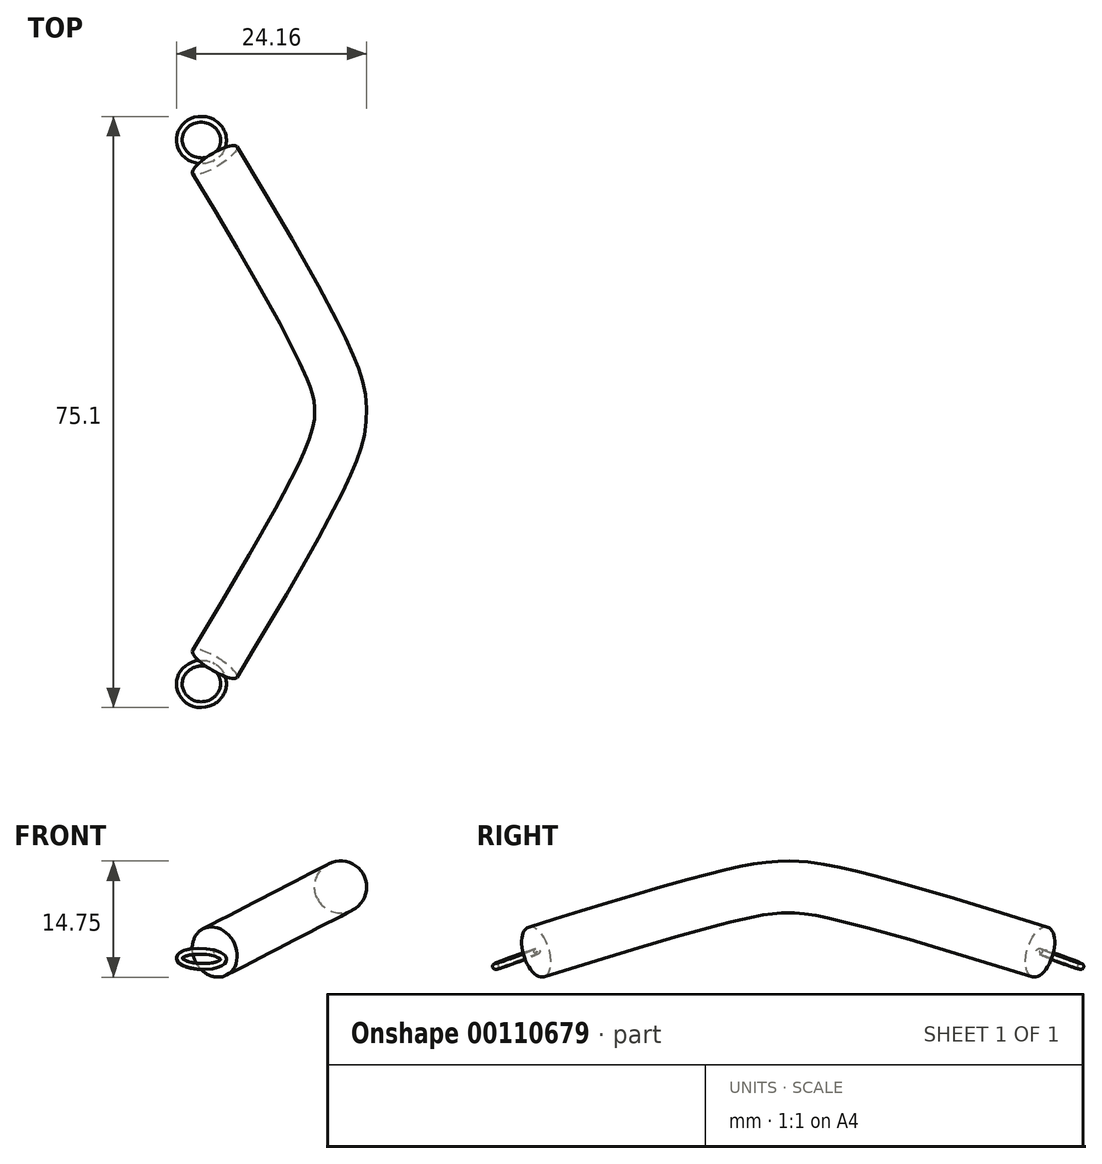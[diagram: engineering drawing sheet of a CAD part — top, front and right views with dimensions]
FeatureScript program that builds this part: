
annotation { "Feature Type Name" : "Feature", "Feature Type Description" : "" }
export const myFeature = defineFeature(function(context is Context, id is Id, definition is map)
    precondition{}
    {
        {
            var Q0;
            Q0=qCreatedBy(makeId("Top.planeOp"),FACE);
            var sketch = newSketch(context, id + "F0", { "sketchPlane" : qUnion([Q0])});
            skLineSegment(sketch, "E0", {"start": v(0, 0) * mm, "end": v(120, 0) * mm, "construction": true});
            skLineSegment(sketch, "E1", {"start": v(102, -32) * mm, "end": v(102, 32) * mm, "construction": true});
            skPoint(sketch, "E2", {"position": v(102, 0) * mm});
            skFitSpline(sketch, "E3", {"points": [v(102, -32) * mm, v(120, 0) * mm, v(102, 32) * mm], "startDerivative": vector(102, 150) * mm, "endDerivative": vector(-102, 150) * mm});
            skLineSegment(sketch, "E4", {"start": v(102, -32) * mm, "end": v(98.2, -37.09) * mm, "construction": true});
            skLineSegment(sketch, "E5", {"start": v(102, 32) * mm, "end": v(98.2, 37.09) * mm, "construction": true});
            skSolve(sketch);
        }
        {
            var Q0;
            Q0=sQuery(id+"F0.wireOp",EDGE,"E3");
            var Q1;
            Q1=sQuery(id+"F0.wireOp",VERTEX,"E1.start");
            cPlane(context, id + "F1", {"entities" : qUnion([Q0, Q1]), "cplaneType" : CPlaneType.CURVE_POINT, "offset" : 150 * mm, "width" : 150 * mm, "height" : 150 * mm});
        }
        {
            var Q0;
            Q0=qCreatedBy(id+"F1.planeOp",FACE);
            var sketch = newSketch(context, id + "F2", { "sketchPlane" : qUnion([Q0])});
            skPoint(sketch, "E6.0", {"position": v(-102.34, 0) * mm});
            skCircle(sketch, "E7", {"center": v(-102.34, 0) * mm, "radius": 3.3 * mm});
            skSolve(sketch);
        }
        {
            var Q0;
            Q0=makeQuery(id+"F2.imprint","IMPRINT",FACE,{"disambiguationData":[TD([[makeQuery(id+"F2.imprint","IMPRINT",EDGE,{"derivedFrom":sQuery(id+"F2.wireOp",EDGE,"E7")}),1.0]])]});
            var Q1;
            Q1=sQuery(id+"F0.wireOp",EDGE,"E3");
            sweep(context, id + "F3", {"profiles" : qUnion([Q0]), "path" : qUnion([Q1])});
        }
        {
            var Q0;
            Q0=makeQuery(id+"F3.opSweep","CAP_FACE",FACE,{"disambiguationData":[OSD([sQuery(id+"F0.wireOp",VERTEX,"E3.start"),sQuery(id+"F2.wireOp",EDGE,"E7")])],"isStart":true});
            var sketch = newSketch(context, id + "F4", { "sketchPlane" : qUnion([Q0])});
            skPoint(sketch, "E8.0", {"position": v(102.34, 0) * mm});
            skCircle(sketch, "E9.0", {"center": v(102.34, 0) * mm, "radius": 3.3 * mm});
            skLineSegment(sketch, "E10", {"start": v(102.34, 0) * mm, "end": v(107.85, 7.87) * mm, "construction": true});
            skLineSegment(sketch, "E11", {"start": v(102.34, 0) * mm, "end": v(102.34, 12) * mm, "construction": true});
            skSolve(sketch);
        }
        {
            var Q0;
            Q0=sQuery(id+"F4.wireOp",EDGE,"E10");
            var Q1;
            Q1=sQuery(id+"F0.wireOp",EDGE,"E4");
            cPlane(context, id + "F5", {"entities" : qUnion([Q0, Q1]), "cplaneType" : CPlaneType.LINE_ANGLE, "offset" : 150 * mm, "angle" : 0 * degree, "width" : 150 * mm, "height" : 150 * mm});
        }
        {
            var Q0;
            Q0=qCreatedBy(id+"F5.planeOp",FACE);
            var sketch = newSketch(context, id + "F6", { "sketchPlane" : qUnion([Q0])});
            skLineSegment(sketch, "E12.0", {"start": v(9.79, 67.09) * mm, "end": v(3.95, 64.59) * mm, "construction": true});
            skCircle(sketch, "E13", {"center": v(4.29, 64.73) * mm, "radius": 0.37 * mm});
            skLineSegment(sketch, "E14", {"start": v(6.87, 65.84) * mm, "end": v(5.34, 69.4) * mm, "construction": true});
            skSolve(sketch);
        }
        {
            var Q0;
            Q0=makeQuery(id+"F6.imprint","IMPRINT",FACE,{"disambiguationData":[TD([[makeQuery(id+"F6.imprint","IMPRINT",EDGE,{"derivedFrom":sQuery(id+"F6.wireOp",EDGE,"E13")}),1.0]])]});
            var Q1;
            Q1=sQuery(id+"F6.wireOp",EDGE,"E14");
            revolve(context, id + "F7", {"entities" : qUnion([Q0]), "axis" : qUnion([Q1]), "revolveType" : RevolveType.FULL});
        }
        {
            var Q0;
            Q0=makeQuery(id+"F7.opRevolve","SWEPT_BODY",BODY,{"disambiguationData":[OSD([sQuery(id+"F6.wireOp",EDGE,"E13")])]});
            var Q1;
            Q1=qCreatedBy(makeId("Front.planeOp"),FACE);
            mirror(context, id + "F8", {"operationType" : NewBodyOperationType.ADD, "entities" : qUnion([Q0]), "mirrorPlane" : qUnion([Q1])});
        }
        {
            var Q0;
            Q0=makeQuery(id+"F3.opSweep","SWEPT_BODY",BODY,{"disambiguationData":[OSD([sQuery(id+"F0.wireOp",EDGE,"E3"),sQuery(id+"F2.wireOp",EDGE,"E7")])]});
            var Q1;
            Q1=sQuery(id+"F0.wireOp",VERTEX,"E3.1.internal");
            var Q2;
            Q2=sQuery(id+"F0.wireOp",EDGE,"E1");
            transform(context, id + "F9", {"entities" : qUnion([Q0]), "transformType" : TransformType.ROTATION, "transformAxis" : qUnion([Q2]), "angle" : 27.3 * degree, "oppositeDirection" : true, "makeCopy" : false});
        }
        {
            var Q0;
            Q0=makeQuery(id+"F3.opSweep","SWEPT_BODY",BODY,{"disambiguationData":[OSD([sQuery(id+"F0.wireOp",EDGE,"E3"),sQuery(id+"F2.wireOp",EDGE,"E7")])]});
            transform(context, id + "F10", {"entities" : qUnion([Q0]), "transformType" : TransformType.TRANSLATION_3D, "dx" : 6.52 * mm, "dy" : 0 * mm, "dz" : -12.58 * mm, "makeCopy" : false});
        }
    });
